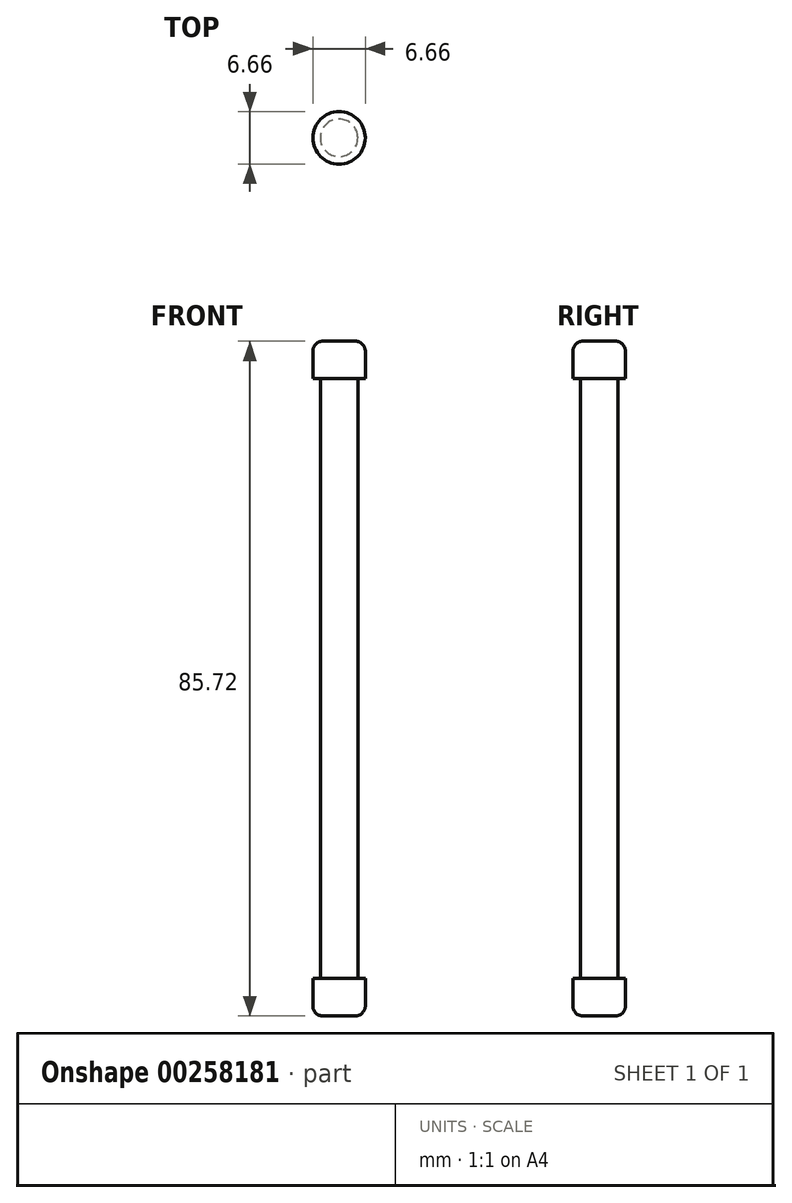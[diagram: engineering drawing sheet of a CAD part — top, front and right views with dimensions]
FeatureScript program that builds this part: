
annotation { "Feature Type Name" : "Feature", "Feature Type Description" : "" }
export const myFeature = defineFeature(function(context is Context, id is Id, definition is map)
    precondition{}
    {
        {
            var Q0;
            Q0=qCreatedBy(makeId("Top.planeOp"),FACE);
            var sketch = newSketch(context, id + "F0", { "sketchPlane" : qUnion([Q0])});
            skCircle(sketch, "E0", {"center": v(0, 0) * mm, "radius": 2.38 * mm});
            skSolve(sketch);
        }
        {
            var Q0;
            Q0=makeQuery(id+"F0.imprint","IMPRINT",FACE,{"disambiguationData":[TD([[makeQuery(id+"F0.imprint","IMPRINT",EDGE,{"derivedFrom":sQuery(id+"F0.wireOp",EDGE,"E0")}),1.0]])]});
            extrude(context, id + "F1", {"entities" : qUnion([Q0]), "depth" : 76.2 * mm});
        }
        {
            var Q0;
            Q0=makeQuery(id+"F1.opExtrude","CAP_FACE",FACE,{"disambiguationData":[OSD([sQuery(id+"F0.wireOp",EDGE,"E0")])],"isStart":false});
            var sketch = newSketch(context, id + "F2", { "sketchPlane" : qUnion([Q0])});
            skCircle(sketch, "E1", {"center": v(0, 0) * mm, "radius": 3.33 * mm});
            skSolve(sketch);
        }
        {
            var Q0;
            Q0 = qSketchRegion(id + "F2", true);
            extrude(context, id + "F3", {"entities" : qUnion([Q0]), "operationType" : NewBodyOperationType.ADD, "depth" : 4.76 * mm});
        }
        {
            var Q0;
            Q0=makeQuery(id+"F1.opExtrude","CAP_FACE",FACE,{"disambiguationData":[OSD([sQuery(id+"F0.wireOp",EDGE,"E0")])],"isStart":true});
            var sketch = newSketch(context, id + "F4", { "sketchPlane" : qUnion([Q0])});
            skCircle(sketch, "E2", {"center": v(0, 0) * mm, "radius": 3.33 * mm});
            skSolve(sketch);
        }
        {
            var Q0;
            Q0 = qSketchRegion(id + "F4", true);
            extrude(context, id + "F5", {"entities" : qUnion([Q0]), "operationType" : NewBodyOperationType.ADD, "depth" : 4.76 * mm});
        }
        {
            var Q0;
            Q0=makeQuery(id+"F5.opExtrude","CAP_FACE",FACE,{"disambiguationData":[OSD([sQuery(id+"F4.wireOp",EDGE,"E2")])],"isStart":false});
            var Q1;
            Q1=makeQuery(id+"F3.opExtrude","CAP_FACE",FACE,{"disambiguationData":[OSD([sQuery(id+"F2.wireOp",EDGE,"E1")])],"isStart":false});
            fillet(context, id + "F6", {"entities" : qUnion([Q0, Q1]), "radius" : 1.27 * mm, "tangentPropagation" : true, "allowEdgeOverflow" : false});
        }
    });
